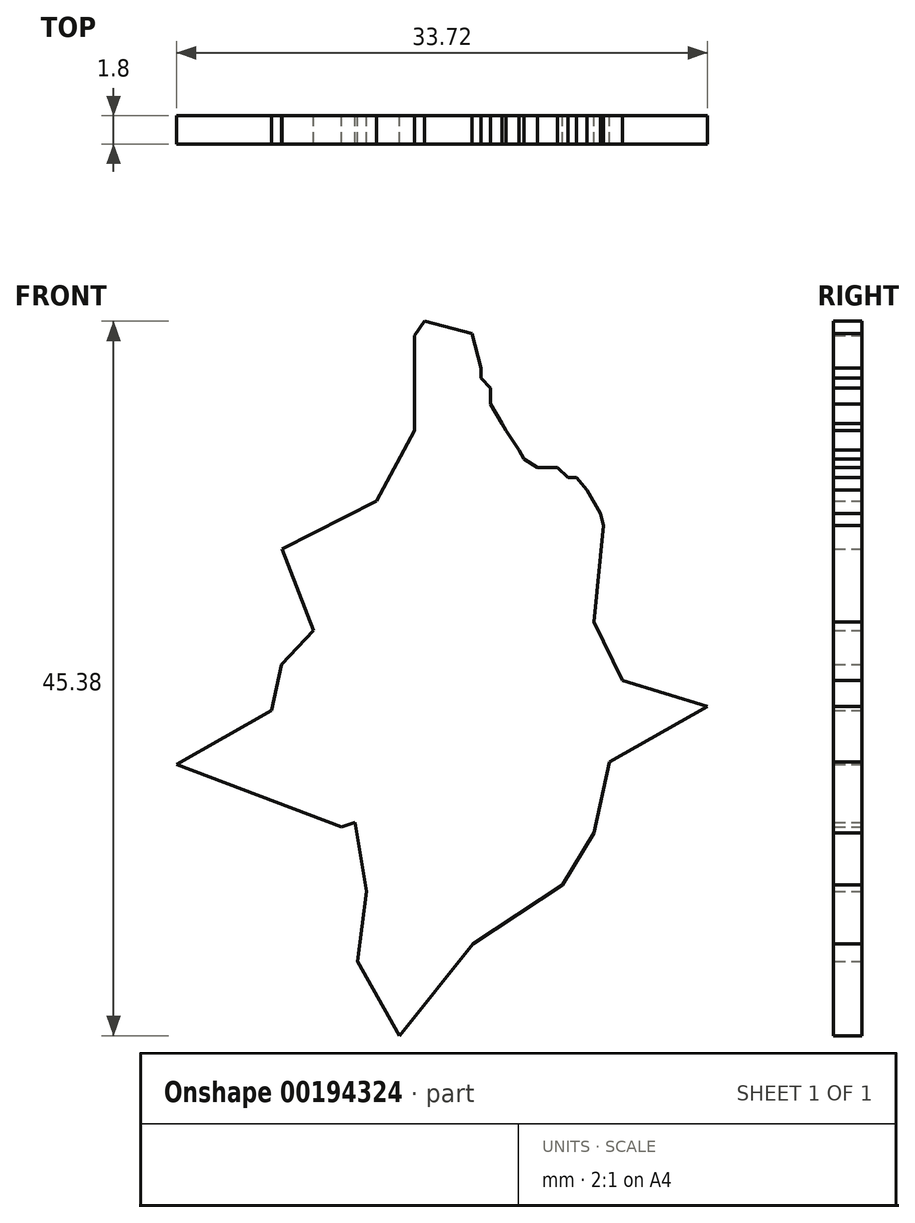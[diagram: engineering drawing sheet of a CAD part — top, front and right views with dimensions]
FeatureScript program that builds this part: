
annotation { "Feature Type Name" : "Feature", "Feature Type Description" : "" }
export const myFeature = defineFeature(function(context is Context, id is Id, definition is map)
    precondition{}
    {
        {
            var Q0;
            Q0=qCreatedBy(makeId("Front.planeOp"),FACE);
            var sketch = newSketch(context, id + "F0", { "sketchPlane" : qUnion([Q0])});
            skLineSegment(sketch, "E0", {"start": v(-3.64, 39.6) * mm, "end": v(1.4, 38.3) * mm});
            skLineSegment(sketch, "E1", {"start": v(1.4, 38.3) * mm, "end": v(2.35, 34.63) * mm});
            skLineSegment(sketch, "E2", {"start": v(2.35, 34.63) * mm, "end": v(2.35, 33.62) * mm});
            skLineSegment(sketch, "E3", {"start": v(2.35, 33.62) * mm, "end": v(3.37, 32.54) * mm});
            skLineSegment(sketch, "E4", {"start": v(3.37, 32.54) * mm, "end": v(3.37, 30.85) * mm});
            skLineSegment(sketch, "E5", {"start": v(3.37, 30.85) * mm, "end": v(4.55, 28.76) * mm});
            skLineSegment(sketch, "E6", {"start": v(4.55, 28.76) * mm, "end": v(5, 28.03) * mm});
            skLineSegment(sketch, "E7", {"start": v(5, 28.03) * mm, "end": v(6.36, 26) * mm});
            skLineSegment(sketch, "E8", {"start": v(6.36, 26) * mm, "end": v(6.92, 25.02) * mm});
            skLineSegment(sketch, "E9", {"start": v(6.92, 25.02) * mm, "end": v(8.34, 24.13) * mm});
            skLineSegment(sketch, "E10", {"start": v(8.34, 24.13) * mm, "end": v(10.43, 24.13) * mm});
            skLineSegment(sketch, "E11", {"start": v(10.43, 24.13) * mm, "end": v(11.56, 23.05) * mm});
            skLineSegment(sketch, "E12", {"start": v(11.56, 23.05) * mm, "end": v(12.46, 23.05) * mm});
            skLineSegment(sketch, "E13", {"start": v(12.46, 23.05) * mm, "end": v(13.56, 21.75) * mm});
            skLineSegment(sketch, "E14", {"start": v(13.56, 21.75) * mm, "end": v(14.32, 20.42) * mm});
            skLineSegment(sketch, "E15", {"start": v(14.32, 20.42) * mm, "end": v(14.98, 19.25) * mm});
            skLineSegment(sketch, "E16", {"start": v(14.98, 19.25) * mm, "end": v(15.3, 18) * mm});
            skLineSegment(sketch, "E17", {"start": v(15.3, 18) * mm, "end": v(14.32, 7.76) * mm});
            skLineSegment(sketch, "E18", {"start": v(14.32, 7.76) * mm, "end": v(17.31, 1.56) * mm});
            skLineSegment(sketch, "E19", {"start": v(17.31, 1.56) * mm, "end": v(26.32, -1.15) * mm});
            skLineSegment(sketch, "E20", {"start": v(26.32, -1.15) * mm, "end": v(15.96, -7.03) * mm});
            skLineSegment(sketch, "E21", {"start": v(15.96, -7.03) * mm, "end": v(14.32, -14.58) * mm});
            skLineSegment(sketch, "E22", {"start": v(14.32, -14.58) * mm, "end": v(11, -20.07) * mm});
            skLineSegment(sketch, "E23", {"start": v(11, -20.07) * mm, "end": v(1.49, -26.31) * mm});
            skLineSegment(sketch, "E24", {"start": v(1.49, -26.31) * mm, "end": v(-6.28, -36.02) * mm});
            skLineSegment(sketch, "E25", {"start": v(-6.28, -36.02) * mm, "end": v(-10.72, -28.18) * mm});
            skLineSegment(sketch, "E26", {"start": v(-10.72, -28.18) * mm, "end": v(-9.75, -20.77) * mm});
            skLineSegment(sketch, "E27", {"start": v(-9.75, -20.77) * mm, "end": v(-11, -13.47) * mm});
            skLineSegment(sketch, "E28", {"start": v(-11, -13.47) * mm, "end": v(-12.4, -13.92) * mm});
            skLineSegment(sketch, "E29", {"start": v(-12.4, -13.92) * mm, "end": v(-29.89, -7.33) * mm});
            skLineSegment(sketch, "E30", {"start": v(-29.89, -7.33) * mm, "end": v(-19.8, -1.6) * mm});
            skLineSegment(sketch, "E31", {"start": v(-19.8, -1.6) * mm, "end": v(-18.74, 3.26) * mm});
            skLineSegment(sketch, "E32", {"start": v(-18.74, 3.26) * mm, "end": v(-15.36, 6.85) * mm});
            skLineSegment(sketch, "E33", {"start": v(-15.36, 6.85) * mm, "end": v(-18.73, 15.49) * mm});
            skLineSegment(sketch, "E34", {"start": v(-18.73, 15.49) * mm, "end": v(-8.7, 20.57) * mm});
            skLineSegment(sketch, "E35", {"start": v(-8.7, 20.57) * mm, "end": v(-4.66, 28.05) * mm});
            skLineSegment(sketch, "E36", {"start": v(-4.66, 28.05) * mm, "end": v(-4.66, 38.08) * mm});
            skLineSegment(sketch, "E37", {"start": v(-4.66, 38.08) * mm, "end": v(-3.64, 39.6) * mm});
            skSolve(sketch);
        }
        {
            var Q0;
            Q0=makeQuery(id+"F0.imprint","IMPRINT",FACE,{"disambiguationData":[TD([[makeQuery(id+"F0.imprint","IMPRINT",EDGE,{"derivedFrom":sQuery(id+"F0.wireOp",EDGE,"E0")}),-1.0]])]});
            extrude(context, id + "F1", {"entities" : qUnion([Q0]), "depth" : 3 * mm});
        }
        {
            var Q0;
            Q0=makeQuery(id+"F1.opExtrude","SWEPT_BODY",BODY,{"disambiguationData":[OSD([sQuery(id+"F0.wireOp",EDGE,"E0"),sQuery(id+"F0.wireOp",EDGE,"E1"),sQuery(id+"F0.wireOp",EDGE,"E2"),sQuery(id+"F0.wireOp",EDGE,"E3"),sQuery(id+"F0.wireOp",EDGE,"E4"),sQuery(id+"F0.wireOp",EDGE,"E5"),sQuery(id+"F0.wireOp",EDGE,"E6"),sQuery(id+"F0.wireOp",EDGE,"E7"),sQuery(id+"F0.wireOp",EDGE,"E8"),sQuery(id+"F0.wireOp",EDGE,"E9"),sQuery(id+"F0.wireOp",EDGE,"E10"),sQuery(id+"F0.wireOp",EDGE,"E11"),sQuery(id+"F0.wireOp",EDGE,"E12"),sQuery(id+"F0.wireOp",EDGE,"E13"),sQuery(id+"F0.wireOp",EDGE,"E14"),sQuery(id+"F0.wireOp",EDGE,"E15"),sQuery(id+"F0.wireOp",EDGE,"E16"),sQuery(id+"F0.wireOp",EDGE,"E17"),sQuery(id+"F0.wireOp",EDGE,"E18"),sQuery(id+"F0.wireOp",EDGE,"E19"),sQuery(id+"F0.wireOp",EDGE,"E20"),sQuery(id+"F0.wireOp",EDGE,"E21"),sQuery(id+"F0.wireOp",EDGE,"E22"),sQuery(id+"F0.wireOp",EDGE,"E23"),sQuery(id+"F0.wireOp",EDGE,"E24"),sQuery(id+"F0.wireOp",EDGE,"E25"),sQuery(id+"F0.wireOp",EDGE,"E26"),sQuery(id+"F0.wireOp",EDGE,"E27"),sQuery(id+"F0.wireOp",EDGE,"E28"),sQuery(id+"F0.wireOp",EDGE,"E29"),sQuery(id+"F0.wireOp",EDGE,"E30"),sQuery(id+"F0.wireOp",EDGE,"E31"),sQuery(id+"F0.wireOp",EDGE,"E32"),sQuery(id+"F0.wireOp",EDGE,"E33"),sQuery(id+"F0.wireOp",EDGE,"E34"),sQuery(id+"F0.wireOp",EDGE,"E35"),sQuery(id+"F0.wireOp",EDGE,"E36"),sQuery(id+"F0.wireOp",EDGE,"E37")])]});
            var Q1;
            Q1=makeQuery(id+"F1.opExtrude","CAP_VERTEX",VERTEX,{"disambiguationData":[OSD([sQuery(id+"F0.wireOp",EDGE,"E24"),sQuery(id+"F0.wireOp",EDGE,"E25")])],"isStart":false});
            transform(context, id + "F2", {"entities" : qUnion([Q0]), "transformType" : TransformType.SCALE_UNIFORMLY, "scale" : 0.6, "scalePoint" : qUnion([Q1]), "makeCopy" : false});
        }
    });
